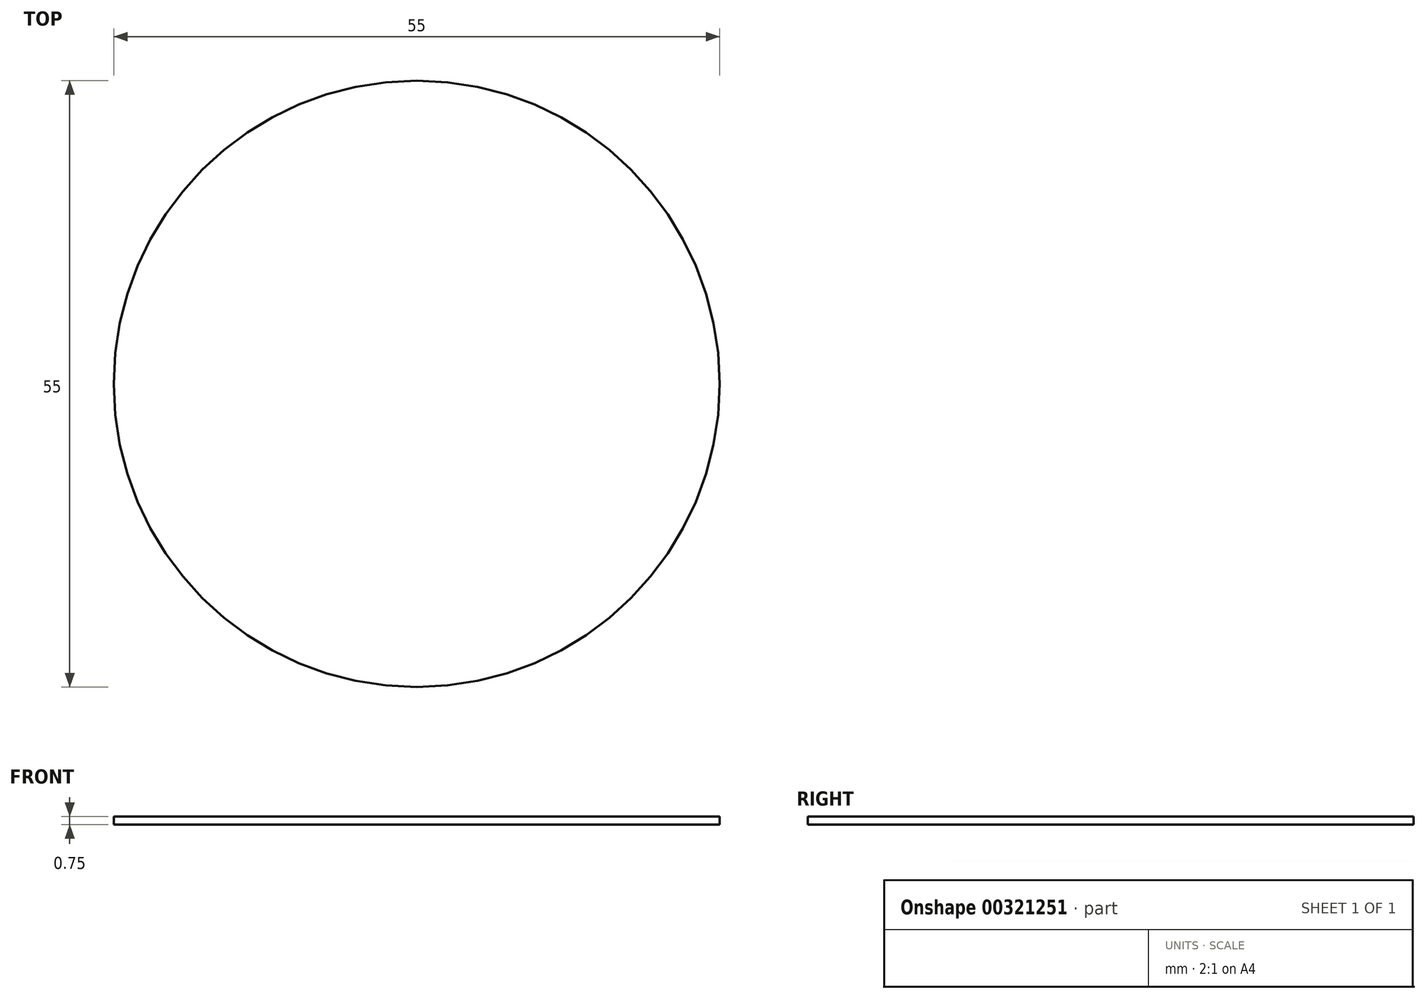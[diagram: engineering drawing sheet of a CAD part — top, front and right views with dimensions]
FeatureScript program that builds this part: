
annotation { "Feature Type Name" : "Feature", "Feature Type Description" : "" }
export const myFeature = defineFeature(function(context is Context, id is Id, definition is map)
    precondition{}
    {
        {
            var Q0;
            Q0=qCreatedBy(makeId("Top.planeOp"),FACE);
            var sketch = newSketch(context, id + "F0", { "sketchPlane" : qUnion([Q0])});
            skCircle(sketch, "E0", {"center": v(0, 0) * mm, "radius": 27.5 * mm});
            skSolve(sketch);
        }
        {
            var Q0;
            Q0 = qSketchRegion(id + "F0", true);
            extrude(context, id + "F1", {"entities" : qUnion([Q0]), "depth" : 0.75 * mm});
        }
    });
